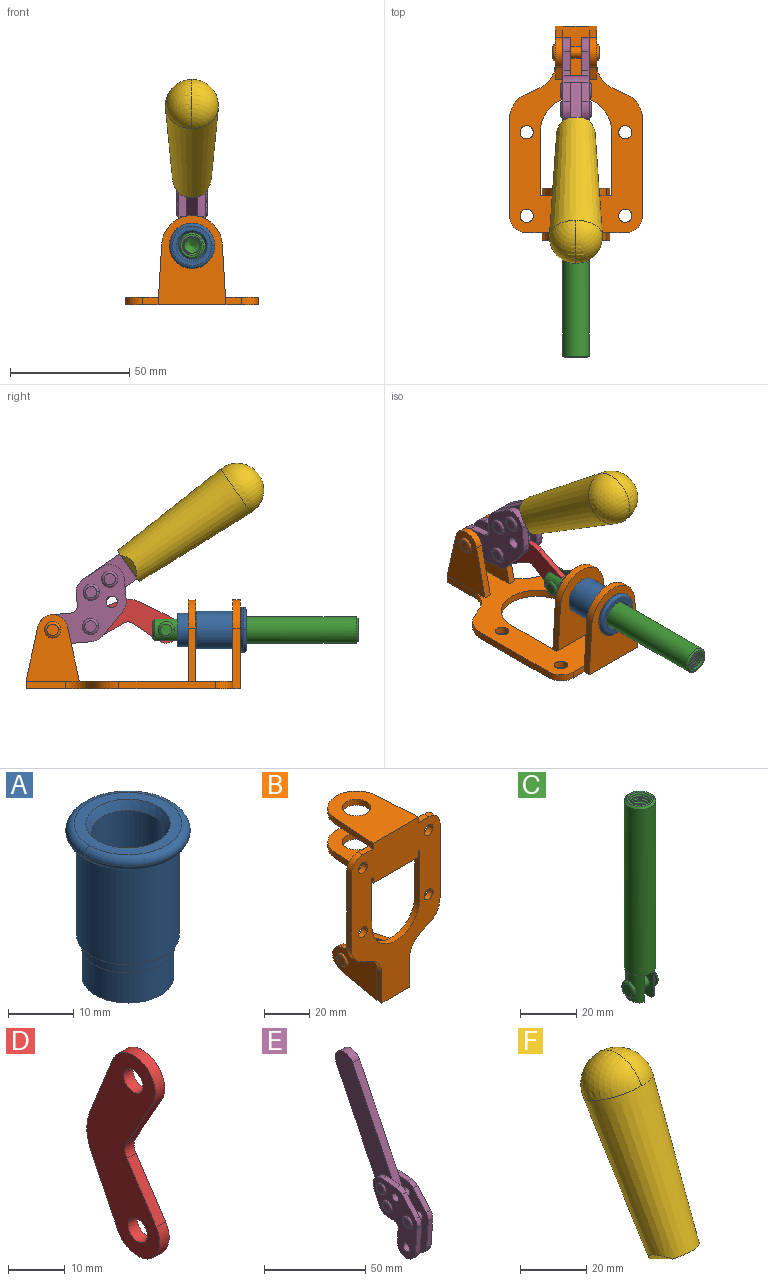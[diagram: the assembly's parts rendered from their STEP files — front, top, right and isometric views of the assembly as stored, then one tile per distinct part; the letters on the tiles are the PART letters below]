
ASSEMBLY  parts=6 mates=6
PART A: 15 faces, bbox 20.6x20.6x28.7 mm
  f0: torus R=8.26mm, axis (0,0,1), area 56.8mm2, adj f1,f10,f12
  f1: torus R=8.26mm, axis (0,0,1), area 56.8mm2, adj f0,f6,f13
  f2: cylinder r=5.59mm len=25.91mm, axis (0,0,1), area 909.6mm2, adj f3,f4
  f3: cone r=6.86mm half-angle=45deg, axis (0,0,-1), area 70.2mm2, adj f2,f14
  f4: cone r=6.47mm half-angle=30deg, axis (0,0,1), area 66.7mm2, adj f2,f13
  f5: cylinder r=7.04mm len=14.07mm, axis (0,0,1), area 252.6mm2, adj f11,f14
  f6: torus R=8.26mm, axis (0,0,1), area 56.8mm2, adj f1,f12,f13
  f7: cylinder r=7.16mm len=14.33mm, axis (0,0,1), area 91.5mm2, adj f9,f11
  f8: cylinder r=7.86mm len=18.42mm, axis (0,0,1), area 909.6mm2, adj f9,f10
  f9: plane 15.72x15.72mm, normal (0,0,-1), area 33mm2, adj f7,f8
  f10: plane 16.51x16.51mm, normal (0,0,-1), area 19.9mm2, adj f0,f8,f12
  f11: plane 14.33x14.33mm, normal (0,0,-1), area 5.7mm2, adj f5,f7
  f12: torus R=8.26mm, axis (0,0,1), area 56.8mm2, adj f0,f6,f10
  f13: plane 16.51x16.51mm, normal (0,0,1), area 82.7mm2, adj f1,f4,f6
  f14: plane 14.07x14.07mm, normal (0,0,-1), area 7.8mm2, adj f3,f5
PART B: 55 faces, bbox 55.7x37.4x89.8 mm
  f0: torus R=2.41mm, axis (-1,0,0), area 15mm2, adj f11,f15,f25
  f1: torus R=2.41mm, axis (-1,0,0), area 15mm2, adj f10,f12,f22
  f2: cylinder r=2.78mm len=5.56mm, axis (0,-1,0), area 54.2mm2, adj f30,f54
  f3: cylinder r=14.99mm len=29.97mm, axis (0,-1,0), area 145.9mm2, adj f30,f49,f53,f54
  f4: cylinder r=2.78mm len=5.56mm, axis (0,-1,0), area 54.2mm2, adj f30,f54
  f5: cylinder r=2.78mm len=5.56mm, axis (0,-1,0), area 54.2mm2, adj f30,f54
  f6: cylinder r=2.78mm len=5.56mm, axis (0,-1,0), area 54.2mm2, adj f30,f54
  f7: cylinder r=6.35mm len=12.7mm, axis (0,0,1), area 123.6mm2, adj f27,f51
  f8: cylinder r=6.35mm len=12.7mm, axis (0,0,-1), area 124.7mm2, adj f21,f35
  f9: cylinder r=2.41mm len=11.18mm, axis (-1,0,0), area 169.4mm2, adj f16,f19
  f10: plane 4.83x4.83mm, normal (1,0,0), area 18.3mm2, adj f1,f12
  f11: plane 4.83x4.83mm, normal (-1,0,0), area 18.3mm2, adj f0,f15
  f12: torus R=2.41mm, axis (-1,0,0), area 15mm2, adj f1,f10,f22
  f13: cylinder r=6.35mm len=12.41mm, axis (1,0,0), area 53.4mm2, adj f18,f19,f22,f23
  f14: cylinder r=6.35mm len=12.41mm, axis (-1,0,0), area 53.4mm2, adj f16,f17,f24,f25
  f15: torus R=2.41mm, axis (-1,0,0), area 15mm2, adj f0,f11,f25
  f16: plane 27.86x22.35mm, normal (1,0,0), area 425.4mm2, adj f9,f14,f17,f24,f30
  f17: plane 22.86x4.97mm, normal (0,0.21,0.98), area 72.5mm2, adj f14,f16,f25,f30
  f18: plane 22.86x4.97mm, normal (0,0.21,0.98), area 72.5mm2, adj f13,f19,f22,f30
  f19: plane 27.86x22.35mm, normal (-1,0,0), area 425.4mm2, adj f9,f13,f18,f23,f30
  f20: cylinder r=12.7mm len=25.35mm, axis (0,0,-1), area 119.8mm2, adj f21,f34,f35,f36
  f21: plane 34.21x28.07mm, normal (0,0,-1), area 702.4mm2, adj f8,f20,f30,f34,f36
  f22: plane 27.96x22.45mm, normal (1,0,0), area 407.2mm2, adj f1,f12,f13,f18,f23,f30,f42,f43
  f23: plane 22.86x4.97mm, normal (0,0.21,-0.98), area 72.5mm2, adj f13,f19,f22,f44
  f24: plane 22.86x4.97mm, normal (0,0.21,-0.98), area 72.5mm2, adj f14,f16,f25,f44
  f25: plane 27.86x22.35mm, normal (-1,0,0), area 407.1mm2, adj f0,f14,f15,f17,f24,f30,f45,f46
  f26: plane 3.1x0.95mm, normal (0,0,-1), area 2.7mm2, adj f30,f49,f50,f54
  f27: plane 34.21x28.07mm, normal (0,0,1), area 702.4mm2, adj f7,f28,f30,f50,f52
  f28: cylinder r=12.7mm len=25.35mm, axis (0,0,1), area 118.8mm2, adj f27,f50,f51,f52
  f29: plane 3.1x0.95mm, normal (0,0,-1), area 2.7mm2, adj f30,f52,f53,f54
  f30: plane 86.54x55.63mm, normal (0,1,0), area 2362.9mm2, adj f2,f3,f4,f5,f6,f16,f17,f18
  f31: plane 40.56x3.1mm, normal (-1,0,0), area 125.7mm2, adj f30,f32,f48,f54
  f32: cylinder r=7.11mm len=7.11mm, axis (0,-1,0), area 34.6mm2, adj f30,f31,f33,f54
  f33: plane 6.67x3.1mm, normal (0,0,1), area 20.4mm2, adj f30,f32,f34,f54
  f34: plane 25.39x3.13mm, normal (-1,0.06,0), area 79.5mm2, adj f20,f21,f33,f35,f54
  f35: plane 37.31x28.45mm, normal (0,0,1), area 789.9mm2, adj f8,f20,f34,f36,f54
  f36: plane 25.39x3.13mm, normal (1,0.06,0), area 79.5mm2, adj f20,f21,f35,f37,f54
  f37: plane 6.67x3.1mm, normal (0,0,1), area 20.4mm2, adj f30,f36,f38,f54
  f38: cylinder r=7.11mm len=7.11mm, axis (0,-1,0), area 34.6mm2, adj f30,f37,f39,f54
  f39: plane 40.56x3.1mm, normal (1,0,0), area 125.7mm2, adj f30,f38,f40,f54
  f40: cylinder r=11.18mm len=10.16mm, axis (0,-1,0), area 39.5mm2, adj f30,f39,f41,f54
  f41: plane 6.09x3.1mm, normal (0.42,0,-0.91), area 20.8mm2, adj f30,f40,f42,f54
  f42: cylinder r=11.18mm len=9.41mm, axis (0,-1,0), area 37.2mm2, adj f22,f30,f41,f43,f54
  f43: plane 16.5x3.1mm, normal (1,0,0), area 51.1mm2, adj f22,f42,f44,f54
  f44: plane 17.37x3.1mm, normal (0,0,-1), area 53.8mm2, adj f23,f24,f30,f43,f45,f54
  f45: plane 16.5x3.1mm, normal (-1,0,0), area 51.1mm2, adj f25,f44,f46,f54
  f46: cylinder r=11.18mm len=9.41mm, axis (0,-1,0), area 37.2mm2, adj f25,f30,f45,f47,f54
  f47: plane 6.09x3.1mm, normal (-0.42,0,-0.91), area 20.8mm2, adj f30,f46,f48,f54
  f48: cylinder r=11.18mm len=10.16mm, axis (0,-1,0), area 39.5mm2, adj f30,f31,f47,f54
  f49: plane 26.54x3.1mm, normal (-1,0,0), area 82.3mm2, adj f3,f26,f30,f54
  f50: plane 25.39x3.1mm, normal (1,0.06,0), area 78.8mm2, adj f26,f27,f28,f51,f54
  f51: plane 37.31x28.45mm, normal (0,0,-1), area 789.9mm2, adj f7,f28,f50,f52,f54
  f52: plane 25.39x3.1mm, normal (-1,0.06,0), area 78.8mm2, adj f27,f28,f29,f51,f54
  f53: plane 26.54x3.1mm, normal (1,0,0), area 82.3mm2, adj f3,f29,f30,f54
  f54: plane 89.66x55.63mm, normal (0,-1,0), area 2678.5mm2, adj f2,f3,f4,f5,f6,f26,f29,f31
PART C: 48 faces, bbox 12.6x11.1x86.1 mm
  f0: torus R=2.41mm, axis (-1,0,0), area 15mm2, adj f30,f32,f34
  f1: torus R=2.41mm, axis (-1,0,0), area 15mm2, adj f29,f31,f33
  f2: cylinder r=5.54mm len=72.39mm, axis (0,0,1), area 2518.5mm2, adj f3,f4,f42,f43
  f3: cone r=5.54mm half-angle=45deg, axis (0,0,1), area 7.6mm2, adj f2,f5,f41
  f4: cone r=5.54mm half-angle=45deg, axis (0,0,-1), area 34.9mm2, adj f2,f39
  f5: cylinder r=5.08mm len=11.48mm, axis (0,0,1), area 108.3mm2, adj f3,f7,f8,f41
  f6: cylinder r=2.41mm len=4.83mm, axis (-1,0,0), area 71.2mm2, adj f40,f41
  f7: cylinder r=2.41mm len=4.83mm, axis (-1,0,0), area 7.6mm2, adj f5,f34
  f8: cone r=5.08mm half-angle=45deg, axis (0,0,1), area 10.6mm2, adj f5,f37,f41
  f9: cone r=3.98mm half-angle=45deg, axis (0,0,1), area 17.6mm2, adj f27,f39,f45,f46,f47
  f10: cylinder r=2.41mm len=4.83mm, axis (-1,0,0), area 7.6mm2, adj f33,f38
  f11: cylinder r=3.2mm len=6.4mm, axis (0,0,1), area 78.4mm2, adj f12,f28,f44,f45,f47
  f12: cylinder r=3.2mm len=6.4mm, axis (0,0,1), area 10.5mm2, adj f11,f13,f45,f47
  f13: cylinder r=3.2mm len=6.4mm, axis (0,0,1), area 10.5mm2, adj f12,f14,f45,f47
  f14: cylinder r=3.2mm len=6.4mm, axis (0,0,1), area 10.5mm2, adj f13,f15,f45,f47
  f15: cylinder r=3.2mm len=6.4mm, axis (0,0,1), area 10.5mm2, adj f14,f16,f45,f47
  f16: cylinder r=3.2mm len=6.4mm, axis (0,0,1), area 10.5mm2, adj f15,f17,f45,f47
  f17: cylinder r=3.2mm len=6.4mm, axis (0,0,1), area 10.5mm2, adj f16,f18,f45,f47
  f18: cylinder r=3.2mm len=6.4mm, axis (0,0,1), area 10.5mm2, adj f17,f19,f45,f47
  f19: cylinder r=3.2mm len=6.4mm, axis (0,0,1), area 10.5mm2, adj f18,f20,f45,f47
  f20: cylinder r=3.2mm len=6.4mm, axis (0,0,1), area 10.5mm2, adj f19,f21,f45,f47
  f21: cylinder r=3.2mm len=6.4mm, axis (0,0,1), area 10.5mm2, adj f20,f22,f45,f47
  f22: cylinder r=3.2mm len=6.4mm, axis (0,0,1), area 10.5mm2, adj f21,f23,f45,f47
  f23: cylinder r=3.2mm len=6.4mm, axis (0,0,1), area 10.5mm2, adj f22,f24,f45,f47
  f24: cylinder r=3.2mm len=6.4mm, axis (0,0,1), area 10.5mm2, adj f23,f25,f45,f47
  f25: cylinder r=3.2mm len=6.4mm, axis (0,0,1), area 10.5mm2, adj f24,f26,f45,f47
  f26: cylinder r=3.2mm len=6.4mm, axis (0,0,1), area 10.5mm2, adj f25,f27,f45,f47
  f27: cylinder r=3.2mm len=6.4mm, axis (0,0,1), area 7.4mm2, adj f9,f26,f45,f47
  f28: cone r=3.2mm half-angle=60deg, axis (0,0,1), area 37.2mm2, adj f11
  f29: plane 4.83x4.83mm, normal (-1,0,0), area 18.3mm2, adj f1,f31
  f30: plane 4.83x4.83mm, normal (1,0,0), area 18.3mm2, adj f0,f32
  f31: torus R=2.41mm, axis (-1,0,0), area 15mm2, adj f1,f29,f33
  f32: torus R=2.41mm, axis (-1,0,0), area 15mm2, adj f0,f30,f34
  f33: plane 6.83x6.83mm, normal (1,0,0), area 18.3mm2, adj f1,f10,f31
  f34: plane 6.83x6.83mm, normal (-1,0,0), area 18.3mm2, adj f0,f7,f32
  f35: cone r=5.08mm half-angle=45deg, axis (0,0,1), area 10.6mm2, adj f36,f38,f40
  f36: plane 7.25x1.97mm, normal (0,0,-1), area 10mm2, adj f35,f40
  f37: plane 7.25x1.97mm, normal (0,0,-1), area 10mm2, adj f8,f41
  f38: cylinder r=5.08mm len=11.48mm, axis (0,0,1), area 108.3mm2, adj f10,f35,f40,f42
  f39: plane 9.55x9.55mm, normal (0,0,1), area 22mm2, adj f4,f9
  f40: plane 12.76x10.09mm, normal (1,0,0), area 95.7mm2, adj f6,f35,f36,f38,f42,f43
  f41: plane 12.76x10.09mm, normal (-1,0,0), area 95.7mm2, adj f3,f5,f6,f8,f37,f43
  f42: cone r=5.54mm half-angle=45deg, axis (0,0,1), area 7.6mm2, adj f2,f38,f40
  f43: plane 11.07x4.7mm, normal (0,0,-1), area 50.4mm2, adj f2,f40,f41
  f44: plane 0.89x0.62mm, normal (-1,0,0), area 0.3mm2, adj f11,f45,f46,f47
  f45: bspline ~24.8x7.63mm, area 266.6mm2, adj f9,f11,f12,f13,f14,f15,f16,f17
  f46: bspline ~24.87x7.63mm, area 73.6mm2, adj f9,f44,f45,f47
  f47: bspline ~24.98x7.63mm, area 272.5mm2, adj f9,f11,f12,f13,f14,f15,f16,f17
PART D: 12 faces, bbox 2.3x18.2x42.8 mm
  f0: cylinder r=2.4mm len=4.8mm, axis (1,0,0), area 34.9mm2, adj f4,f11
  f1: cylinder r=10.41mm len=8.47mm, axis (1,0,0), area 20.2mm2, adj f4,f9,f10,f11
  f2: cylinder r=3.05mm len=3.16mm, axis (1,0,0), area 7.7mm2, adj f4,f6,f7,f11
  f3: cylinder r=2.4mm len=4.8mm, axis (1,0,0), area 34.9mm2, adj f4,f11
  f4: plane 42.81x18.23mm, normal (-1,0,0), area 414.1mm2, adj f0,f1,f2,f3,f5,f6,f7,f8
  f5: cylinder r=5.54mm len=10.67mm, axis (1,0,0), area 41.8mm2, adj f4,f6,f10,f11
  f6: plane 11.66x6.53mm, normal (0,-0.87,-0.49), area 30.9mm2, adj f2,f4,f5,f11
  f7: plane 11.17x7.33mm, normal (0,-0.84,0.55), area 30.9mm2, adj f2,f4,f8,f11
  f8: cylinder r=5.54mm len=10.51mm, axis (1,0,0), area 41.8mm2, adj f4,f7,f9,f11
  f9: plane 13.67x6.67mm, normal (0,0.9,-0.44), area 35.1mm2, adj f1,f4,f8,f11
  f10: plane 14.1x5.7mm, normal (0,0.93,0.37), area 35.1mm2, adj f1,f4,f5,f11
  f11: plane 42.81x18.23mm, normal (1,0,0), area 414.1mm2, adj f0,f1,f2,f3,f5,f6,f7,f8
PART E: 59 faces, bbox 12.9x60.2x99.6 mm
  f0: torus R=2.39mm, axis (-1,0,0), area 14.9mm2, adj f20,f43,f51
  f1: torus R=2.39mm, axis (-1,0,0), area 14.9mm2, adj f19,f42,f51
  f2: torus R=2.39mm, axis (-1,0,0), area 14.9mm2, adj f18,f35,f51
  f3: torus R=2.39mm, axis (-1,0,0), area 14.9mm2, adj f14,f17,f23
  f4: torus R=2.39mm, axis (-1,0,0), area 14.9mm2, adj f13,f16,f23
  f5: torus R=2.39mm, axis (-1,0,0), area 14.9mm2, adj f12,f15,f23
  f6: cylinder r=2.39mm len=4.78mm, axis (1,0,0), area 46.5mm2, adj f48,f50,f51
  f7: cylinder r=2.39mm len=4.78mm, axis (1,0,0), area 46.5mm2, adj f50,f51
  f8: cylinder r=6.35mm len=12.68mm, axis (1,0,0), area 61.8mm2, adj f38,f39,f50,f51
  f9: cylinder r=2.39mm len=4.78mm, axis (-1,0,0), area 70.5mm2, adj f46,f50
  f10: cylinder r=2.39mm len=4.78mm, axis (-1,0,0), area 46.5mm2, adj f23,f45,f46
  f11: cylinder r=2.39mm len=4.78mm, axis (-1,0,0), area 46.5mm2, adj f23,f46
  f12: plane 4.78x4.78mm, normal (1,0,0), area 17.9mm2, adj f5,f15
  f13: plane 4.78x4.78mm, normal (1,0,0), area 17.9mm2, adj f4,f16
  f14: plane 4.78x4.78mm, normal (1,0,0), area 17.9mm2, adj f3,f17
  f15: torus R=2.39mm, axis (-1,0,0), area 14.9mm2, adj f5,f12,f23
  f16: torus R=2.39mm, axis (-1,0,0), area 14.9mm2, adj f4,f13,f23
  f17: torus R=2.39mm, axis (-1,0,0), area 14.9mm2, adj f3,f14,f23
  f18: plane 4.78x4.78mm, normal (-1,0,0), area 17.9mm2, adj f2,f35
  f19: plane 4.78x4.78mm, normal (-1,0,0), area 17.9mm2, adj f1,f42
  f20: plane 4.78x4.78mm, normal (-1,0,0), area 17.9mm2, adj f0,f43
  f21: plane 2.26x0.2mm, normal (1,0,0), area 0.2mm2, adj f31,f44
  f22: plane 2.26x0.2mm, normal (-1,0,0), area 0.2mm2, adj f41,f44
  f23: plane 39.37x30.77mm, normal (1,0,0), area 565.5mm2, adj f3,f4,f5,f10,f11,f15,f16,f17
  f24: cylinder r=6.1mm len=4.15mm, axis (-1,0,0), area 14.7mm2, adj f23,f25,f32,f46
  f25: plane 10.25x9.01mm, normal (0,-0.75,0.66), area 42.3mm2, adj f23,f24,f26,f46
  f26: cylinder r=6.35mm len=4.64mm, axis (-1,0,0), area 15.6mm2, adj f23,f25,f27,f46
  f27: plane 15.84x3.1mm, normal (0,-1,-0.07), area 49.2mm2, adj f23,f26,f28,f46
  f28: cylinder r=6.35mm len=12.68mm, axis (-1,0,0), area 61.8mm2, adj f23,f27,f29,f46
  f29: plane 8.11x3.1mm, normal (0,1,0.07), area 25.2mm2, adj f23,f28,f30,f46
  f30: cylinder r=3.05mm len=3.25mm, axis (-1,0,0), area 14.8mm2, adj f23,f29,f31,f46
  f31: plane 5.99x3.1mm, normal (0,0.07,-1), area 18.6mm2, adj f21,f23,f30,f44,f46
  f32: plane 9.5x3.1mm, normal (0,-0.07,1), area 29.5mm2, adj f23,f24,f33,f46,f47
  f33: cylinder r=6.1mm len=8.63mm, axis (-1,0,0), area 39.1mm2, adj f23,f32,f34,f47
  f34: plane 8.65x3.96mm, normal (0,0.91,-0.42), area 29.5mm2, adj f23,f33,f44,f47
  f35: torus R=2.39mm, axis (-1,0,0), area 14.9mm2, adj f2,f18,f51
  f36: plane 10.25x9.01mm, normal (0,-0.75,0.66), area 42.3mm2, adj f37,f49,f50,f51
  f37: cylinder r=6.35mm len=4.64mm, axis (1,0,0), area 15.6mm2, adj f36,f38,f50,f51
  f38: plane 15.84x3.1mm, normal (0,-1,-0.07), area 49.2mm2, adj f8,f37,f50,f51
  f39: plane 8.11x3.1mm, normal (0,1,0.07), area 25.2mm2, adj f8,f40,f50,f51
  f40: cylinder r=3.05mm len=3.25mm, axis (1,0,0), area 14.8mm2, adj f39,f41,f50,f51
  f41: plane 5.99x3.1mm, normal (0,0.07,-1), area 18.6mm2, adj f22,f40,f44,f50,f51
  f42: torus R=2.39mm, axis (-1,0,0), area 14.9mm2, adj f1,f19,f51
  f43: torus R=2.39mm, axis (-1,0,0), area 14.9mm2, adj f0,f20,f51
  f44: cylinder r=6.35mm len=12.12mm, axis (-1,0,0), area 128.9mm2, adj f21,f22,f23,f31,f34,f41,f46,f47
  f45: plane 2.65x1.35mm, normal (1,0,0), area 1mm2, adj f10,f55
  f46: plane 39.08x20.42mm, normal (-1,0,0), area 412.5mm2, adj f9,f10,f11,f24,f25,f26,f27,f28
  f47: plane 77.62x39.82mm, normal (1,0,0), area 850mm2, adj f32,f33,f34,f44,f53,f54,f55
  f48: plane 2.65x1.35mm, normal (-1,0,0), area 1mm2, adj f6,f55
  f49: cylinder r=6.1mm len=4.15mm, axis (1,0,0), area 14.7mm2, adj f36,f50,f51,f56
  f50: plane 39.08x20.42mm, normal (1,0,0), area 412.5mm2, adj f6,f7,f8,f9,f36,f37,f38,f39
  f51: plane 39.37x30.77mm, normal (-1,0,0), area 565.5mm2, adj f0,f1,f2,f6,f7,f8,f35,f36
  f52: plane 8.65x3.96mm, normal (0,0.91,-0.42), area 29.5mm2, adj f44,f51,f57,f58
  f53: plane 68.49x33.4mm, normal (0,0.9,-0.44), area 358.1mm2, adj f44,f47,f54,f58
  f54: cylinder r=6.35mm len=12.06mm, axis (1,0,0), area 93.7mm2, adj f47,f53,f55,f58
  f55: plane 68.49x33.4mm, normal (0,-0.9,0.44), area 358.1mm2, adj f44,f45,f46,f47,f48,f50,f54,f58
  f56: plane 9.5x3.1mm, normal (0,-0.07,1), area 29.5mm2, adj f49,f50,f51,f57,f58
  f57: cylinder r=6.1mm len=8.63mm, axis (1,0,0), area 39.1mm2, adj f51,f52,f56,f58
  f58: plane 77.62x39.82mm, normal (-1,0,0), area 850mm2, adj f44,f52,f53,f54,f55,f56,f57
PART F: 11 faces, bbox 22.3x42.6x64.5 mm
  f0: sphere r=11.13mm, area 411.4mm2, adj f1,f8
  f1: cone r=11.11mm half-angle=3.3deg, axis (0,0.44,0.9), area 3251.8mm2, adj f0,f7,f8,f9,f10
  f2: cylinder r=6.16mm len=11.7mm, axis (1,0,0), area 89.5mm2, adj f3,f4,f5,f6
  f3: plane 60.23x36.75mm, normal (-1,0,0), area 763.6mm2, adj f2,f4,f6,f10
  f4: plane 51.37x25.05mm, normal (0,0.9,-0.44), area 264.2mm2, adj f2,f3,f5,f10
  f5: plane 60.23x36.75mm, normal (1,0,0), area 763.6mm2, adj f2,f4,f6,f10
  f6: plane 51.37x25.05mm, normal (0,-0.9,0.44), area 264.2mm2, adj f2,f3,f5,f10
  f7: plane 9.95x5.95mm, normal (0.71,-0.31,-0.64), area 25.8mm2, adj f1,f10
  f8: sphere r=11.13mm, area 411.4mm2, adj f0,f1
  f9: plane 9.95x5.95mm, normal (-0.71,-0.31,-0.64), area 25.8mm2, adj f1,f10
  f10: plane 14.27x11.38mm, normal (0,-0.44,-0.9), area 106.7mm2, adj f1,f3,f4,f5,f6,f7,f9
PLACE A rot(axis=(1,0,0),90deg) t=(0,9.43,0)mm
PLACE B rot(axis=(1,0,0),90deg) t=(0,9.43,0)mm fixed
PLACE C rot(axis=(1,0,0),90deg) t=(0,9.46,0)mm
PLACE D rot(axis=(0,-0.7,-0.71),180deg) t=(-1.16,10.46,1.26)mm
PLACE E rot(axis=(1,0,0),81deg) t=(0,5.96,5.35)mm
PLACE F rot(axis=(1,0,0),81deg) t=(-0.04,5.96,5.35)mm
MATE revolute C.f6 <-> D.f3  axis (-1,0,0) through (0,-6.01,24.61)mm
MATE fastened A.f2 <-> B.f7  axis (0,1,0) through (0,-36.96,24.61)mm
MATE revolute E.f4 <-> D.f0  axis (-1,0,0) through (0,25.71,26.01)mm
MATE fastened F.f2 <-> E.f54  axis (1,0,0) through (-2.35,-36.97,84.11)mm
MATE slider C.f2 <-> A.f2  axis (0,-1,0) through (0,-49.32,24.61)mm
MATE revolute E.f7 <-> B.f0  axis (-1,0,0) through (0,41.52,24.61)mm
